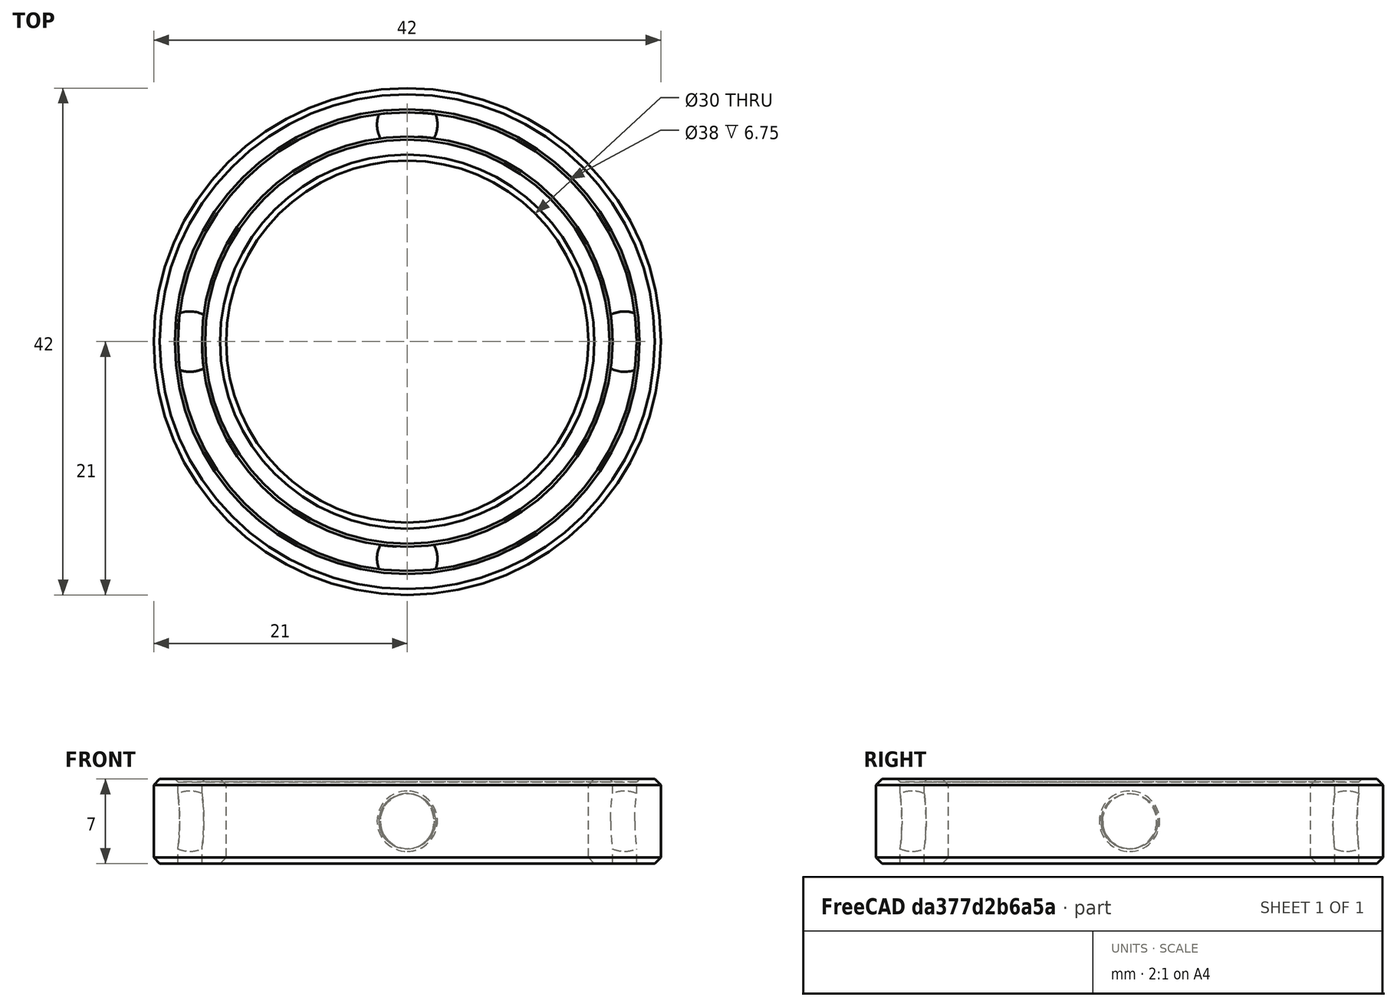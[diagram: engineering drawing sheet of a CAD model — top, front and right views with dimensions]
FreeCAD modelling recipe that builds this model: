
FCSTD DOCUMENT
Label: ballrace30x42x7
License: CC-BY 3.0
LicenseURL: http://creativecommons.org/licenses/by/3.0/
objects: Part::Chamfer×6, Part::Cylinder×4, Part::Sphere×4, Part::Cut×2, Part::MultiFuse×1
note: 17 computed .brp shape members not serialized (recipe doc carries the construction recipe); baked Part::Feature solids carry a one-line shape summary decoded from their .brp

FEATURE [Part::Cylinder] Cylinder  label="Cylinder21R"
  Angle = 360
  Height = 7
  Radius = 21
FEATURE [Part::Cylinder] Cylinder001  label="Cylinder19R"
  Angle = 360
  Height = 10
  Placement = pos=(0,0,-1.5) rot=(0,0,1;0rad)
  Radius = 19
FEATURE [Part::Cut] Cut  label="OuterRace"
  Base = -> Cylinder
  Tool = -> Cylinder001
FEATURE [Part::Cylinder] Cylinder002  label="Cylinder17R"
  Angle = 360
  Height = 7
  Radius = 17
FEATURE [Part::Cylinder] Cylinder003  label="Cylinder15R"
  Angle = 360
  Height = 10
  Radius = 15
FEATURE [Part::Cut] Cut001
  Base = -> Cylinder002
  Tool = -> Cylinder003
FEATURE [Part::Chamfer] Chamfer
  Base = -> Cut
  Edges = 1 edges r=0.5: [Edge1]
FEATURE [Part::Chamfer] Chamfer001
  Base = -> Chamfer
  Edges = 1 edges r=0.5: [Edge3]
FEATURE [Part::Chamfer] Chamfer002
  Base = -> Cut001
  Edges = 1 edges r=0.5: [Edge5]
FEATURE [Part::Chamfer] Chamfer003
  Base = -> Chamfer002
  Edges = 1 edges r=0.5: [Edge11]
FEATURE [Part::Chamfer] Chamfer004
  Base = -> Chamfer003
  Edges = 1 edges r=0.25: [Edge12]
FEATURE [Part::Chamfer] Chamfer005
  Base = -> Chamfer001
  Edges = 1 edges r=0.25: [Edge10]
FEATURE [Part::Sphere] Sphere  label="ballN"
  Angle1 = -90
  Angle2 = 90
  Angle3 = 360
  Placement = pos=(18,0,3.5) rot=(0,0,1;0rad)
  Radius = 2.5
FEATURE [Part::Sphere] Sphere3  label="ballS"
  Angle1 = -90
  Angle2 = 90
  Angle3 = 360
  Placement = pos=(-18,0,3.5) rot=(0,0,1;0rad)
  Radius = 2.5
FEATURE [Part::Sphere] Sphere004  label="ballW"
  Angle1 = -90
  Angle2 = 90
  Angle3 = 360
  Placement = pos=(0,18,3.5) rot=(0,0,1;0rad)
  Radius = 2.5
FEATURE [Part::Sphere] Sphere005  label="ballE"
  Angle1 = -90
  Angle2 = 90
  Angle3 = 360
  Placement = pos=(0,-18,3.5) rot=(0,0,1;0rad)
  Radius = 2.5
FEATURE [Part::MultiFuse] Fusion  label="ballrace30x42x7"
  Shapes = -> [Chamfer004,Chamfer005,Sphere,Sphere3,Sphere004,Sphere005]
